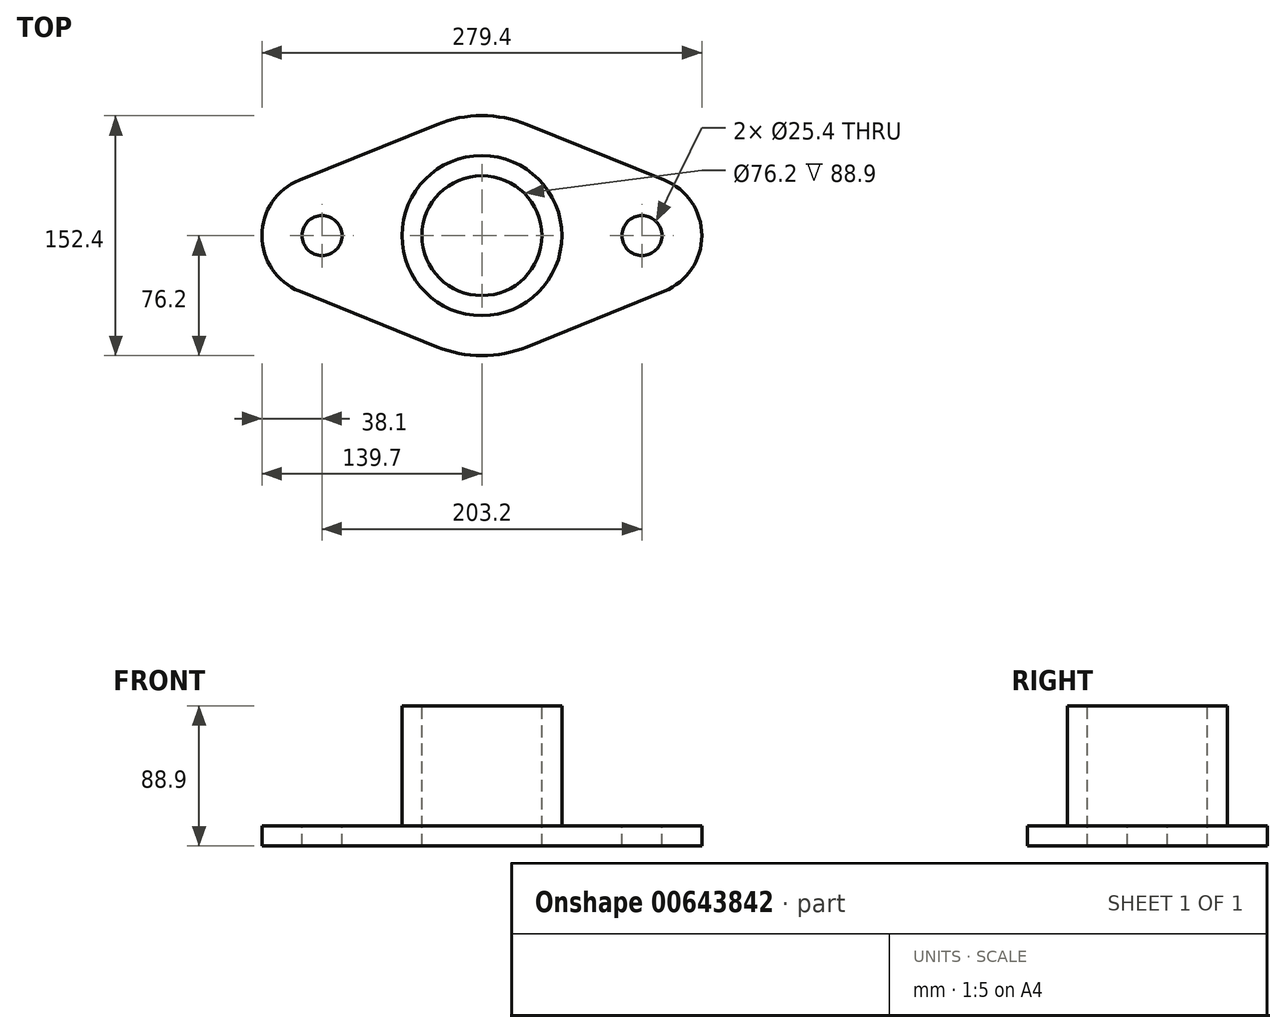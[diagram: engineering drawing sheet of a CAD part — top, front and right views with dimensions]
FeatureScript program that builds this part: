
annotation { "Feature Type Name" : "Feature", "Feature Type Description" : "" }
export const myFeature = defineFeature(function(context is Context, id is Id, definition is map)
    precondition{}
    {
        {
            var Q0;
            Q0=qCreatedBy(makeId("Top.planeOp"),FACE);
            var sketch = newSketch(context, id + "F0", { "sketchPlane" : qUnion([Q0])});
            skArc(sketch, "E0", {"start": v(-28.58, -70.64) * mm, "mid": v(0, -76.2) * mm, "end": v(28.58, -70.64) * mm});
            skArc(sketch, "E1", {"start": v(115.89, -35.32) * mm, "mid": v(139.7, 0) * mm, "end": v(115.89, 35.32) * mm});
            skArc(sketch, "E2", {"start": v(-115.89, 35.32) * mm, "mid": v(-139.7, 0) * mm, "end": v(-115.89, -35.32) * mm});
            skLineSegment(sketch, "E3", {"start": v(-115.89, 35.32) * mm, "end": v(-28.57, 70.64) * mm});
            skLineSegment(sketch, "E4", {"start": v(-115.89, -35.32) * mm, "end": v(-28.57, -70.64) * mm});
            skLineSegment(sketch, "E5", {"start": v(28.57, -70.64) * mm, "end": v(115.89, -35.32) * mm});
            skLineSegment(sketch, "E6", {"start": v(115.89, 35.32) * mm, "end": v(28.57, 70.64) * mm});
            skArc(sketch, "E7.trimOffspring", {"start": v(28.58, 70.64) * mm, "mid": v(0, 76.2) * mm, "end": v(-28.57, 70.64) * mm});
            skSolve(sketch);
        }
        {
            var Q0;
            Q0=makeQuery(id+"F0.imprint","IMPRINT",FACE,{"disambiguationData":[TD([[makeQuery(id+"F0.imprint","IMPRINT",EDGE,{"derivedFrom":sQuery(id+"F0.wireOp",EDGE,"E0")}),1.0]])]});
            extrude(context, id + "F1", {"entities" : qUnion([Q0]), "depth" : 12.7 * mm, "offsetDistance" : 25.4 * mm});
        }
        {
            var Q0;
            Q0=makeQuery(id+"F1.opExtrude","CAP_FACE",FACE,{"disambiguationData":[OSD([sQuery(id+"F0.wireOp",EDGE,"E0"),sQuery(id+"F0.wireOp",EDGE,"E1"),sQuery(id+"F0.wireOp",EDGE,"E2"),sQuery(id+"F0.wireOp",EDGE,"E3"),sQuery(id+"F0.wireOp",EDGE,"E4"),sQuery(id+"F0.wireOp",EDGE,"E5"),sQuery(id+"F0.wireOp",EDGE,"E6"),sQuery(id+"F0.wireOp",EDGE,"E7.trimOffspring")])],"isStart":false});
            var sketch = newSketch(context, id + "F2", { "sketchPlane" : qUnion([Q0])});
            skCircle(sketch, "E8", {"center": v(-101.6, 0) * mm, "radius": 12.7 * mm});
            skSolve(sketch);
        }
        {
            var Q0;
            Q0=makeQuery(id+"F2.imprint","IMPRINT",FACE,{"disambiguationData":[TD([[makeQuery(id+"F2.imprint","IMPRINT",EDGE,{"derivedFrom":sQuery(id+"F2.wireOp",EDGE,"E8")}),1.0]])]});
            extrude(context, id + "F3", {"entities" : qUnion([Q0]), "operationType" : NewBodyOperationType.REMOVE, "endBound" : BoundingType.UP_TO_NEXT, "oppositeDirection" : true, "depth" : 25.4 * mm, "offsetDistance" : 25.4 * mm});
        }
        {
            var Q0;
            Q0=makeQuery(id+"F1.opExtrude","CAP_FACE",FACE,{"disambiguationData":[OSD([sQuery(id+"F0.wireOp",EDGE,"E0"),sQuery(id+"F0.wireOp",EDGE,"E1"),sQuery(id+"F0.wireOp",EDGE,"E2"),sQuery(id+"F0.wireOp",EDGE,"E3"),sQuery(id+"F0.wireOp",EDGE,"E4"),sQuery(id+"F0.wireOp",EDGE,"E5"),sQuery(id+"F0.wireOp",EDGE,"E6"),sQuery(id+"F0.wireOp",EDGE,"E7.trimOffspring")])],"isStart":false});
            var sketch = newSketch(context, id + "F4", { "sketchPlane" : qUnion([Q0])});
            skCircle(sketch, "E9", {"center": v(101.6, 0) * mm, "radius": 12.7 * mm});
            skSolve(sketch);
        }
        {
            var Q0;
            Q0=makeQuery(id+"F4.imprint","IMPRINT",FACE,{"disambiguationData":[TD([[makeQuery(id+"F4.imprint","IMPRINT",EDGE,{"derivedFrom":sQuery(id+"F4.wireOp",EDGE,"E9")}),1.0]])]});
            extrude(context, id + "F5", {"entities" : qUnion([Q0]), "operationType" : NewBodyOperationType.REMOVE, "oppositeDirection" : true, "depth" : 25.4 * mm, "offsetDistance" : 25.4 * mm});
        }
        {
            var Q0;
            Q0=makeQuery(id+"F1.opExtrude","CAP_FACE",FACE,{"disambiguationData":[OSD([sQuery(id+"F0.wireOp",EDGE,"E0"),sQuery(id+"F0.wireOp",EDGE,"E1"),sQuery(id+"F0.wireOp",EDGE,"E2"),sQuery(id+"F0.wireOp",EDGE,"E3"),sQuery(id+"F0.wireOp",EDGE,"E4"),sQuery(id+"F0.wireOp",EDGE,"E5"),sQuery(id+"F0.wireOp",EDGE,"E6"),sQuery(id+"F0.wireOp",EDGE,"E7.trimOffspring")])],"isStart":false});
            var sketch = newSketch(context, id + "F6", { "sketchPlane" : qUnion([Q0])});
            skCircle(sketch, "E10", {"center": v(0, 0) * mm, "radius": 50.8 * mm});
            skSolve(sketch);
        }
        {
            var Q0;
            Q0=makeQuery(id+"F6.imprint","IMPRINT",FACE,{"disambiguationData":[TD([[makeQuery(id+"F6.imprint","IMPRINT",EDGE,{"derivedFrom":sQuery(id+"F6.wireOp",EDGE,"E10")}),1.0]])]});
            extrude(context, id + "F7", {"entities" : qUnion([Q0]), "operationType" : NewBodyOperationType.ADD, "depth" : 76.2 * mm, "offsetDistance" : 25.4 * mm});
        }
        {
            var Q0;
            Q0=makeQuery(id+"F7.opExtrude","CAP_FACE",FACE,{"disambiguationData":[OSD([sQuery(id+"F6.wireOp",EDGE,"E10")])],"isStart":false});
            var sketch = newSketch(context, id + "F8", { "sketchPlane" : qUnion([Q0])});
            skCircle(sketch, "E11", {"center": v(0, 0) * mm, "radius": 38.1 * mm});
            skSolve(sketch);
        }
        {
            var Q0;
            Q0=makeQuery(id+"F8.imprint","IMPRINT",FACE,{"disambiguationData":[TD([[makeQuery(id+"F8.imprint","IMPRINT",EDGE,{"derivedFrom":sQuery(id+"F8.wireOp",EDGE,"E11")}),1.0]])]});
            extrude(context, id + "F9", {"entities" : qUnion([Q0]), "operationType" : NewBodyOperationType.REMOVE, "endBound" : BoundingType.UP_TO_NEXT, "oppositeDirection" : true, "depth" : 25.4 * mm, "offsetDistance" : 25.4 * mm});
        }
    });
